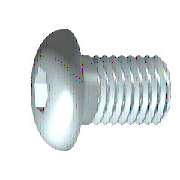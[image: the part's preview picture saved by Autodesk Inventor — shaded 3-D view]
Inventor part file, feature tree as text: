
AUTODESK INVENTOR PART (.ipt)
format: ipt  version: 2023.4 (Build 274418000, 418)  size: 190,464 bytes
history: native  units: mm (DEFAULTED — no unit token found)
features: extrude x1, plane x1, fillet x1
ambient origin geometry x7: Origin, YZ Plane, XY Plane, X Axis, Y Axis, Z Axis, Center Point
bodies: Solid1 (feature_tree), Body (feature_tree)
feature tree (3):
  extrude  "Slot"  Depth=23.2916mm
  plane  "Work Plane1"
  fillet  "Fillet2"  Radius=2.1083mm
